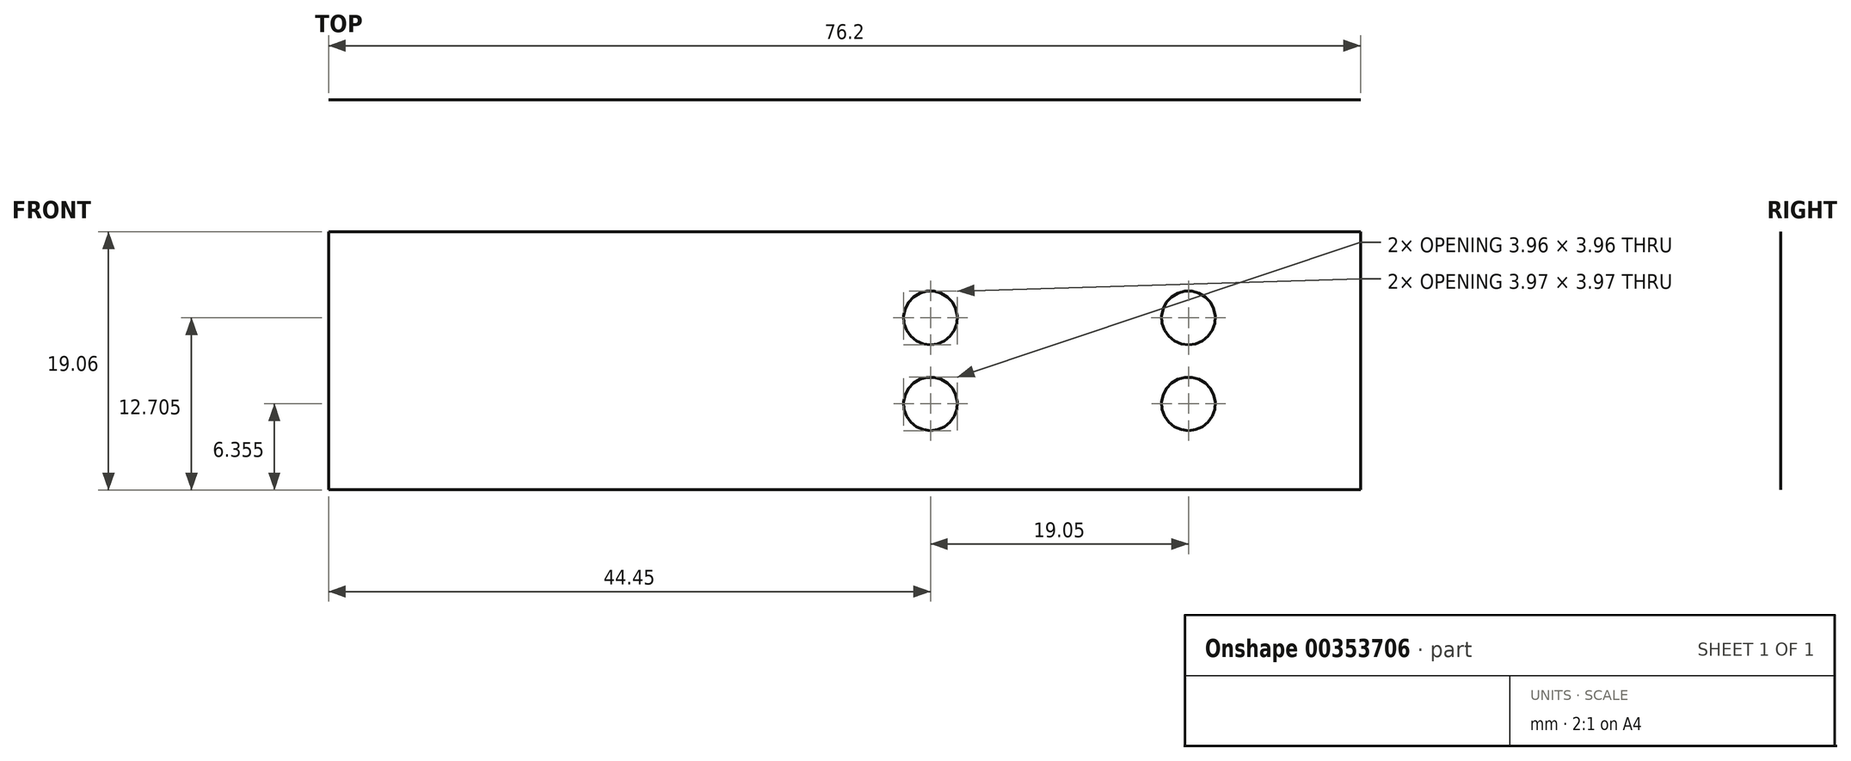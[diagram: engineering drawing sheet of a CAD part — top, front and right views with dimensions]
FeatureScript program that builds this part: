
annotation { "Feature Type Name" : "Feature", "Feature Type Description" : "" }
export const myFeature = defineFeature(function(context is Context, id is Id, definition is map)
    precondition{}
    {
        {
            var Q0;
            Q0=qCreatedBy(makeId("Front.planeOp"),FACE);
            var sketch = newSketch(context, id + "F0", { "sketchPlane" : qUnion([Q0])});
            skLineSegment(sketch, "E0.bottom", {"start": v(38.1, 9.52) * mm, "end": v(-38.1, 9.52) * mm});
            skLineSegment(sketch, "E0.top", {"start": v(38.1, -9.53) * mm, "end": v(-38.1, -9.53) * mm});
            skLineSegment(sketch, "E0.left", {"start": v(38.1, 9.52) * mm, "end": v(38.1, -9.53) * mm});
            skLineSegment(sketch, "E0.right", {"start": v(-38.1, 9.52) * mm, "end": v(-38.1, -9.53) * mm});
            skPoint(sketch, "E0.middle", {"position": v(0, 0) * mm});
            skSolve(sketch);
        }
        {
            var Q0;
            Q0 = qSketchRegion(id + "F0", true);
            extrude(context, id + "F1", {"entities" : qUnion([Q0]), "depth" : 1 / 203.2 * mm, "symmetric" : true});
        }
        {
            var Q0;
            Q0=makeQuery(id+"F1.opExtrude","CAP_FACE",FACE,{"disambiguationData":[OSD([sQuery(id+"F0.wireOp",EDGE,"E0.bottom"),sQuery(id+"F0.wireOp",EDGE,"E0.top"),sQuery(id+"F0.wireOp",EDGE,"E0.left"),sQuery(id+"F0.wireOp",EDGE,"E0.right")])],"isStart":false});
            var sketch = newSketch(context, id + "F2", { "sketchPlane" : qUnion([Q0])});
            skLineSegment(sketch, "E1", {"start": v(38.1, -9.53) * mm, "end": v(25.4, -9.53) * mm, "construction": true});
            skLineSegment(sketch, "E2", {"start": v(25.4, -9.53) * mm, "end": v(25.4, 9.52) * mm, "construction": true});
            skLineSegment(sketch, "E3", {"start": v(25.4, -9.53) * mm, "end": v(6.35, -9.53) * mm, "construction": true});
            skLineSegment(sketch, "E4", {"start": v(6.35, -9.53) * mm, "end": v(6.35, 9.52) * mm, "construction": true});
            skLineSegment(sketch, "E5", {"start": v(-38.1, -9.53) * mm, "end": v(-38.1, -3.18) * mm, "construction": true});
            skLineSegment(sketch, "E6", {"start": v(-38.1, -3.18) * mm, "end": v(38.1, -3.18) * mm, "construction": true});
            skLineSegment(sketch, "E7", {"start": v(-38.1, 9.52) * mm, "end": v(-38.1, 3.17) * mm, "construction": true});
            skLineSegment(sketch, "E8", {"start": v(-38.1, 3.17) * mm, "end": v(38.1, 3.17) * mm, "construction": true});
            skCircle(sketch, "E9", {"center": v(6.35, 3.17) * mm, "radius": 1.98 * mm});
            skCircle(sketch, "E10", {"center": v(6.35, -3.18) * mm, "radius": 1.98 * mm});
            skCircle(sketch, "E11", {"center": v(25.4, 3.17) * mm, "radius": 1.98 * mm});
            skCircle(sketch, "E12", {"center": v(25.4, -3.18) * mm, "radius": 1.98 * mm});
            skSolve(sketch);
        }
        {
            var Q0;
            Q0 = qSketchRegion(id + "F2", true);
            extrude(context, id + "F3", {"entities" : qUnion([Q0]), "operationType" : NewBodyOperationType.REMOVE, "oppositeDirection" : true, "depth" : 3.17 * mm});
        }
        {
            var Q0;
            Q0 = qSketchRegion(id + "F2", true);
            extrude(context, id + "F4", {"entities" : qUnion([Q0]), "operationType" : NewBodyOperationType.REMOVE, "oppositeDirection" : true, "depth" : 3.17 * mm});
        }
    });
